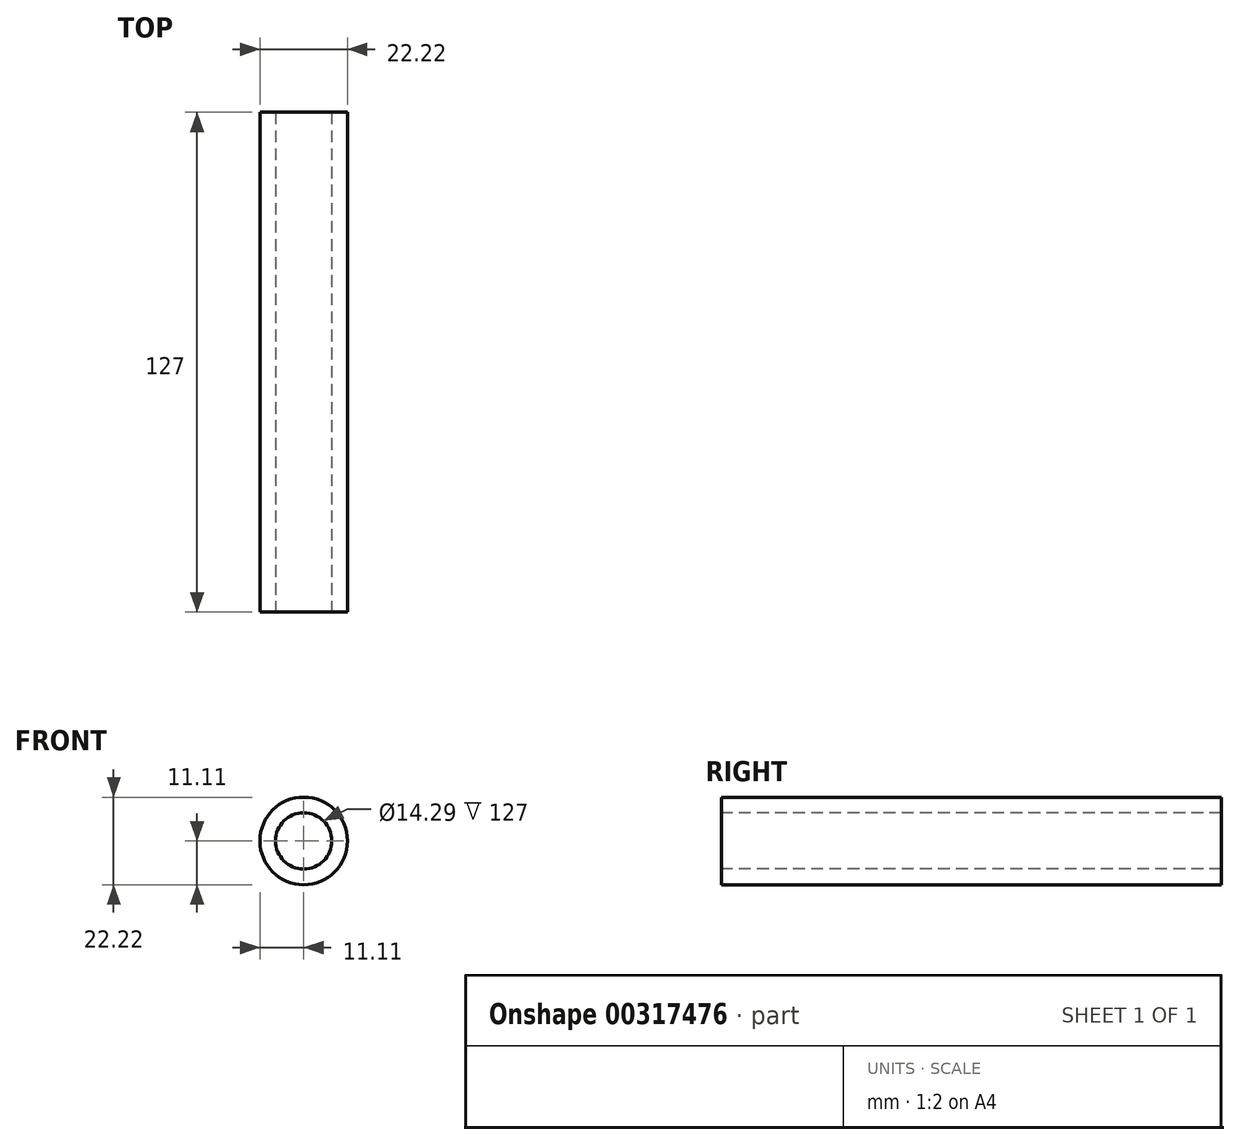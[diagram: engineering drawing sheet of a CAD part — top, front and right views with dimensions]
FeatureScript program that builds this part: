
annotation { "Feature Type Name" : "Feature", "Feature Type Description" : "" }
export const myFeature = defineFeature(function(context is Context, id is Id, definition is map)
    precondition{}
    {
        {
            var Q0;
            Q0=qCreatedBy(makeId("Front.planeOp"),FACE);
            var sketch = newSketch(context, id + "F0", { "sketchPlane" : qUnion([Q0])});
            skCircle(sketch, "E0", {"center": v(0, 0) * mm, "radius": 11.11 * mm});
            skSolve(sketch);
        }
        {
            var Q0;
            Q0=makeQuery(id+"F0.imprint","IMPRINT",FACE,{"disambiguationData":[TD([[makeQuery(id+"F0.imprint","IMPRINT",EDGE,{"derivedFrom":sQuery(id+"F0.wireOp",EDGE,"E0")}),1.0]])]});
            extrude(context, id + "F1", {"entities" : qUnion([Q0]), "endBound" : BoundingType.SYMMETRIC, "depth" : 127 * mm});
        }
        {
            var Q0;
            Q0=makeQuery(id+"F1.opExtrude","CAP_FACE",FACE,{"disambiguationData":[OSD([sQuery(id+"F0.wireOp",EDGE,"E0")])],"isStart":false});
            var sketch = newSketch(context, id + "F2", { "sketchPlane" : qUnion([Q0])});
            skCircle(sketch, "E1", {"center": v(0, 0) * mm, "radius": 7.14 * mm});
            skSolve(sketch);
        }
        {
            var Q0;
            Q0 = qSketchRegion(id + "F2", true);
            extrude(context, id + "F3", {"entities" : qUnion([Q0]), "operationType" : NewBodyOperationType.REMOVE, "oppositeDirection" : true, "depth" : 127 * mm});
        }
    });
